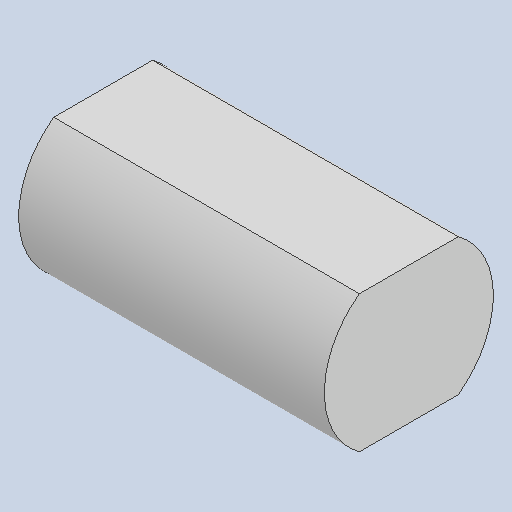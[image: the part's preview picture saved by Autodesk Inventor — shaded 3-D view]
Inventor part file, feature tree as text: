
AUTODESK INVENTOR PART (.ipt)
format: ipt  version: 2022 (Build 260153070, 153G)  size: 89,600 bytes
history: native  units: in
note: dims shown in document units (in); Inventor stores cm internally (conversion verified against a paired STEP export)
features: other x3, sketch x1
ambient origin geometry x8: Origin, YZ Plane, XZ Plane, XY Plane, X Axis, Y Axis, Z Axis, Center Point
bodies: Solid1 (feature_tree)
feature tree (4):
  other  "TTmotor.ipt"
  other  "Solid2::TTmotor.ipt"
  other  "TaggingFeature1"
  sketch  "Sketch1"  dims[d0=0.3937in]
